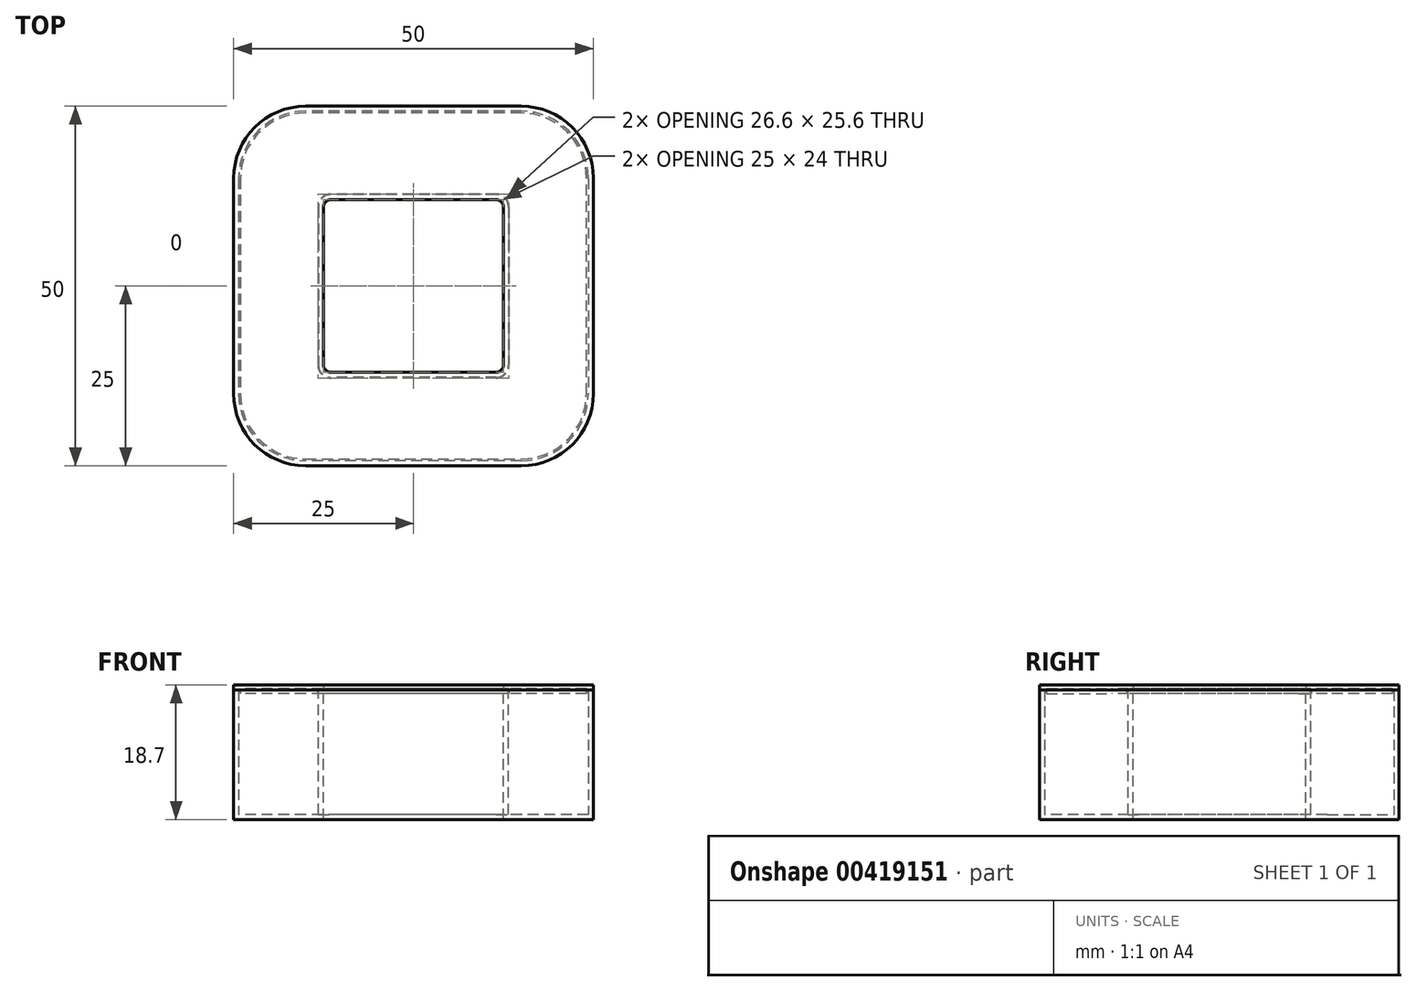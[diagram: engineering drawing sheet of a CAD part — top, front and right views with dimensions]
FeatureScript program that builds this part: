
annotation { "Feature Type Name" : "Feature", "Feature Type Description" : "" }
export const myFeature = defineFeature(function(context is Context, id is Id, definition is map)
    precondition{}
    {
        {
            var Q0;
            Q0=qCreatedBy(makeId("Top.planeOp"),FACE);
            var sketch = newSketch(context, id + "F0", { "sketchPlane" : qUnion([Q0])});
            skLineSegment(sketch, "E0.bottom", {"start": v(15, 25) * mm, "end": v(-15, 25) * mm});
            skLineSegment(sketch, "E0.top", {"start": v(15, -25) * mm, "end": v(-15, -25) * mm});
            skLineSegment(sketch, "E0.left", {"start": v(25, 15) * mm, "end": v(25, -15) * mm});
            skLineSegment(sketch, "E0.right", {"start": v(-25, 15) * mm, "end": v(-25, -15) * mm});
            skPoint(sketch, "E0.middle", {"position": v(0, 0) * mm});
            skPoint(sketch, "E1.visualSharp", {"position": v(-25, 25) * mm});
            skArc(sketch, "E1.filletArc", {"start": v(-15, 25) * mm, "mid": v(-22.07, 22.07) * mm, "end": v(-25, 15) * mm});
            skPoint(sketch, "E2.visualSharp", {"position": v(25, 25) * mm});
            skArc(sketch, "E2.filletArc", {"start": v(25, 15) * mm, "mid": v(22.07, 22.07) * mm, "end": v(15, 25) * mm});
            skPoint(sketch, "E3.visualSharp", {"position": v(25, -25) * mm});
            skArc(sketch, "E3.filletArc", {"start": v(15, -25) * mm, "mid": v(22.07, -22.07) * mm, "end": v(25, -15) * mm});
            skPoint(sketch, "E4.visualSharp", {"position": v(-25, -25) * mm});
            skArc(sketch, "E4.filletArc", {"start": v(-25, -15) * mm, "mid": v(-22.07, -22.07) * mm, "end": v(-15, -25) * mm});
            skSolve(sketch);
        }
        {
            var Q0;
            Q0 = qSketchRegion(id + "F0", true);
            extrude(context, id + "F1", {"entities" : qUnion([Q0]), "depth" : 18 * mm});
        }
        {
            var Q0;
            Q0=makeQuery(id+"F1.opExtrude","CAP_FACE",FACE,{"disambiguationData":[OSD([sQuery(id+"F0.wireOp",EDGE,"E0.bottom"),sQuery(id+"F0.wireOp",EDGE,"E0.top"),sQuery(id+"F0.wireOp",EDGE,"E0.left"),sQuery(id+"F0.wireOp",EDGE,"E0.right"),sQuery(id+"F0.wireOp",EDGE,"E1.filletArc"),sQuery(id+"F0.wireOp",EDGE,"E2.filletArc"),sQuery(id+"F0.wireOp",EDGE,"E3.filletArc"),sQuery(id+"F0.wireOp",EDGE,"E4.filletArc")])],"isStart":false});
            var sketch = newSketch(context, id + "F2", { "sketchPlane" : qUnion([Q0])});
            skLineSegment(sketch, "E5.bottom", {"start": v(11.5, 12) * mm, "end": v(-11.5, 12) * mm});
            skLineSegment(sketch, "E5.top", {"start": v(11.5, -12) * mm, "end": v(-11.5, -12) * mm});
            skLineSegment(sketch, "E5.left", {"start": v(12.5, 11) * mm, "end": v(12.5, -11) * mm});
            skLineSegment(sketch, "E5.right", {"start": v(-12.5, 11) * mm, "end": v(-12.5, -11) * mm});
            skPoint(sketch, "E5.middle", {"position": v(0, 0) * mm});
            skPoint(sketch, "E6.visualSharp", {"position": v(-12.5, 12) * mm});
            skArc(sketch, "E6.filletArc", {"start": v(-11.5, 12) * mm, "mid": v(-12.2, 11.7) * mm, "end": v(-12.5, 11) * mm});
            skPoint(sketch, "E7.visualSharp", {"position": v(12.5, 12) * mm});
            skArc(sketch, "E7.filletArc", {"start": v(12.5, 11) * mm, "mid": v(12.2, 11.7) * mm, "end": v(11.5, 12) * mm});
            skPoint(sketch, "E8.visualSharp", {"position": v(12.5, -12) * mm});
            skArc(sketch, "E8.filletArc", {"start": v(11.5, -12) * mm, "mid": v(12.2, -11.7) * mm, "end": v(12.5, -11) * mm});
            skPoint(sketch, "E9.visualSharp", {"position": v(-12.5, -12) * mm});
            skArc(sketch, "E9.filletArc", {"start": v(-12.5, -11) * mm, "mid": v(-12.2, -11.7) * mm, "end": v(-11.5, -12) * mm});
            skSolve(sketch);
        }
        {
            var Q0;
            Q0=makeQuery(id+"F2.imprint","IMPRINT",FACE,{"disambiguationData":[TD([[makeQuery(id+"F2.imprint","IMPRINT",EDGE,{"derivedFrom":sQuery(id+"F2.wireOp",EDGE,"E5.bottom")}),1.0]])]});
            extrude(context, id + "F3", {"entities" : qUnion([Q0]), "operationType" : NewBodyOperationType.REMOVE, "endBound" : BoundingType.THROUGH_ALL, "oppositeDirection" : true, "depth" : 25 * mm});
        }
        {
            var Q0;
            Q0=makeQuery(id+"F1.opExtrude","CAP_FACE",FACE,{"disambiguationData":[OSD([sQuery(id+"F0.wireOp",EDGE,"E0.bottom"),sQuery(id+"F0.wireOp",EDGE,"E0.top"),sQuery(id+"F0.wireOp",EDGE,"E0.left"),sQuery(id+"F0.wireOp",EDGE,"E0.right"),sQuery(id+"F0.wireOp",EDGE,"E1.filletArc"),sQuery(id+"F0.wireOp",EDGE,"E2.filletArc"),sQuery(id+"F0.wireOp",EDGE,"E3.filletArc"),sQuery(id+"F0.wireOp",EDGE,"E4.filletArc")])],"isStart":false});
            shell(context, id + "F4", {"entities" : qUnion([Q0]), "thickness" : 0.7 * mm});
        }
        {
            var Q0;
            Q0=makeQuery(id+"F1.opExtrude","CAP_FACE",FACE,{"disambiguationData":[OSD([sQuery(id+"F0.wireOp",EDGE,"E0.bottom"),sQuery(id+"F0.wireOp",EDGE,"E0.top"),sQuery(id+"F0.wireOp",EDGE,"E0.left"),sQuery(id+"F0.wireOp",EDGE,"E0.right"),sQuery(id+"F0.wireOp",EDGE,"E1.filletArc"),sQuery(id+"F0.wireOp",EDGE,"E2.filletArc"),sQuery(id+"F0.wireOp",EDGE,"E3.filletArc"),sQuery(id+"F0.wireOp",EDGE,"E4.filletArc")])],"isStart":false});
            var sketch = newSketch(context, id + "F5", { "sketchPlane" : qUnion([Q0])});
            skLineSegment(sketch, "E10.0", {"start": v(-24.3, 15) * mm, "end": v(-24.3, -15) * mm});
            skArc(sketch, "E10.1", {"start": v(-15, 24.3) * mm, "mid": v(-21.58, 21.58) * mm, "end": v(-24.3, 15) * mm});
            skLineSegment(sketch, "E10.2", {"start": v(15, 24.3) * mm, "end": v(-15, 24.3) * mm});
            skArc(sketch, "E10.3", {"start": v(24.3, 15) * mm, "mid": v(21.58, 21.58) * mm, "end": v(15, 24.3) * mm});
            skLineSegment(sketch, "E10.4", {"start": v(24.3, 15) * mm, "end": v(24.3, -15) * mm});
            skArc(sketch, "E10.5", {"start": v(15, -24.3) * mm, "mid": v(21.58, -21.58) * mm, "end": v(24.3, -15) * mm});
            skLineSegment(sketch, "E10.6", {"start": v(15, -24.3) * mm, "end": v(-15, -24.3) * mm});
            skArc(sketch, "E10.7", {"start": v(-24.3, -15) * mm, "mid": v(-21.58, -21.58) * mm, "end": v(-15, -24.3) * mm});
            skLineSegment(sketch, "E10.8", {"start": v(11.5, 12.7) * mm, "end": v(-11.5, 12.7) * mm});
            skArc(sketch, "E10.9", {"start": v(13.2, 11) * mm, "mid": v(12.7, 12.2) * mm, "end": v(11.5, 12.7) * mm});
            skLineSegment(sketch, "E10.10", {"start": v(13.2, 11) * mm, "end": v(13.2, -11) * mm});
            skArc(sketch, "E10.11", {"start": v(11.5, -12.7) * mm, "mid": v(12.7, -12.2) * mm, "end": v(13.2, -11) * mm});
            skLineSegment(sketch, "E10.12", {"start": v(11.5, -12.7) * mm, "end": v(-11.5, -12.7) * mm});
            skArc(sketch, "E10.13", {"start": v(-13.2, -11) * mm, "mid": v(-12.7, -12.2) * mm, "end": v(-11.5, -12.7) * mm});
            skLineSegment(sketch, "E10.14", {"start": v(-13.2, 11) * mm, "end": v(-13.2, -11) * mm});
            skArc(sketch, "E10.15", {"start": v(-11.5, 12.7) * mm, "mid": v(-12.7, 12.2) * mm, "end": v(-13.2, 11) * mm});
            skArc(sketch, "E11.0", {"start": v(23.5, 15) * mm, "mid": v(21.01, 21.01) * mm, "end": v(15, 23.5) * mm});
            skLineSegment(sketch, "E11.1", {"start": v(23.5, 15) * mm, "end": v(23.5, -15) * mm});
            skLineSegment(sketch, "E11.2", {"start": v(15, 23.5) * mm, "end": v(-15, 23.5) * mm});
            skArc(sketch, "E11.3", {"start": v(15, -23.5) * mm, "mid": v(21.01, -21.01) * mm, "end": v(23.5, -15) * mm});
            skArc(sketch, "E11.4", {"start": v(-15, 23.5) * mm, "mid": v(-21.01, 21.01) * mm, "end": v(-23.5, 15) * mm});
            skLineSegment(sketch, "E11.5", {"start": v(-23.5, 15) * mm, "end": v(-23.5, -15) * mm});
            skArc(sketch, "E11.6", {"start": v(-23.5, -15) * mm, "mid": v(-21.01, -21.01) * mm, "end": v(-15, -23.5) * mm});
            skLineSegment(sketch, "E11.7", {"start": v(15, -23.5) * mm, "end": v(-15, -23.5) * mm});
            skArc(sketch, "E12.0", {"start": v(13.3, 11) * mm, "mid": v(12.77, 12.27) * mm, "end": v(11.5, 12.8) * mm});
            skLineSegment(sketch, "E12.1", {"start": v(13.3, 11) * mm, "end": v(13.3, -11) * mm});
            skLineSegment(sketch, "E12.2", {"start": v(11.5, 12.8) * mm, "end": v(-11.5, 12.8) * mm});
            skArc(sketch, "E12.3", {"start": v(11.5, -12.8) * mm, "mid": v(12.77, -12.27) * mm, "end": v(13.3, -11) * mm});
            skArc(sketch, "E12.4", {"start": v(-11.5, 12.8) * mm, "mid": v(-12.77, 12.27) * mm, "end": v(-13.3, 11) * mm});
            skLineSegment(sketch, "E12.5", {"start": v(-13.3, 11) * mm, "end": v(-13.3, -11) * mm});
            skArc(sketch, "E12.6", {"start": v(-13.3, -11) * mm, "mid": v(-12.77, -12.27) * mm, "end": v(-11.5, -12.8) * mm});
            skLineSegment(sketch, "E12.7", {"start": v(11.5, -12.8) * mm, "end": v(-11.5, -12.8) * mm});
            skArc(sketch, "E13.0", {"start": v(-24.05, -15) * mm, "mid": v(-21.4, -21.4) * mm, "end": v(-15, -24.05) * mm});
            skLineSegment(sketch, "E13.1", {"start": v(-24.05, 15) * mm, "end": v(-24.05, -15) * mm});
            skLineSegment(sketch, "E13.2", {"start": v(-15, -24.05) * mm, "end": v(15, -24.05) * mm});
            skArc(sketch, "E13.3", {"start": v(-15, 24.05) * mm, "mid": v(-21.4, 21.4) * mm, "end": v(-24.05, 15) * mm});
            skArc(sketch, "E13.4", {"start": v(15, -24.05) * mm, "mid": v(21.4, -21.4) * mm, "end": v(24.05, -15) * mm});
            skLineSegment(sketch, "E13.5", {"start": v(24.05, -15) * mm, "end": v(24.05, 15) * mm});
            skArc(sketch, "E13.6", {"start": v(24.05, 15) * mm, "mid": v(21.4, 21.4) * mm, "end": v(15, 24.05) * mm});
            skLineSegment(sketch, "E13.7", {"start": v(15, 24.05) * mm, "end": v(-15, 24.05) * mm});
            skSolve(sketch);
        }
        {
            var Q0;
            Q0=makeQuery(id+"F5.imprint","IMPRINT",FACE,{"disambiguationData":[TD([[makeQuery(id+"F5.imprint","IMPRINT",EDGE,{"derivedFrom":sQuery(id+"F5.wireOp",EDGE,"E11.0")}),1.0]])]});
            var Q1;
            Q1=makeQuery(id+"F5.imprint","IMPRINT",FACE,{"disambiguationData":[TD([[makeQuery(id+"F5.imprint","IMPRINT",EDGE,{"derivedFrom":sQuery(id+"F5.wireOp",EDGE,"E11.0")}),-1.0]])]});
            extrude(context, id + "F6", {"entities" : qUnion([Q0, Q1]), "oppositeDirection" : true, "depth" : 0.5 * mm});
        }
        {
            var Q0;
            Q0=makeQuery(id+"F6.opExtrude","CAP_FACE",FACE,{"disambiguationData":[OSD([sQuery(id+"F5.wireOp",EDGE,"E12.0"),sQuery(id+"F5.wireOp",EDGE,"E12.1"),sQuery(id+"F5.wireOp",EDGE,"E12.2"),sQuery(id+"F5.wireOp",EDGE,"E12.3"),sQuery(id+"F5.wireOp",EDGE,"E12.4"),sQuery(id+"F5.wireOp",EDGE,"E12.5"),sQuery(id+"F5.wireOp",EDGE,"E12.6"),sQuery(id+"F5.wireOp",EDGE,"E12.7"),sQuery(id+"F5.wireOp",EDGE,"E13.0"),sQuery(id+"F5.wireOp",EDGE,"E13.1"),sQuery(id+"F5.wireOp",EDGE,"E13.2"),sQuery(id+"F5.wireOp",EDGE,"E13.3"),sQuery(id+"F5.wireOp",EDGE,"E13.4"),sQuery(id+"F5.wireOp",EDGE,"E13.5"),sQuery(id+"F5.wireOp",EDGE,"E13.6"),sQuery(id+"F5.wireOp",EDGE,"E13.7")])],"isStart":true});
            var sketch = newSketch(context, id + "F7", { "sketchPlane" : qUnion([Q0])});
            skArc(sketch, "E14.0", {"start": v(-15, 25) * mm, "mid": v(-22.07, 22.07) * mm, "end": v(-25, 15) * mm});
            skLineSegment(sketch, "E14.1", {"start": v(15, 25) * mm, "end": v(-15, 25) * mm});
            skArc(sketch, "E14.2", {"start": v(25, 15) * mm, "mid": v(22.07, 22.07) * mm, "end": v(15, 25) * mm});
            skLineSegment(sketch, "E14.3", {"start": v(25, 15) * mm, "end": v(25, -15) * mm});
            skArc(sketch, "E14.4", {"start": v(15, -25) * mm, "mid": v(22.07, -22.07) * mm, "end": v(25, -15) * mm});
            skLineSegment(sketch, "E14.5", {"start": v(15, -25) * mm, "end": v(-15, -25) * mm});
            skArc(sketch, "E14.6", {"start": v(-25, -15) * mm, "mid": v(-22.07, -22.07) * mm, "end": v(-15, -25) * mm});
            skLineSegment(sketch, "E14.7", {"start": v(-25, 15) * mm, "end": v(-25, -15) * mm});
            skLineSegment(sketch, "E14.8", {"start": v(-12.5, 11) * mm, "end": v(-12.5, -11) * mm});
            skArc(sketch, "E14.9", {"start": v(-11.5, 12) * mm, "mid": v(-12.2, 11.7) * mm, "end": v(-12.5, 11) * mm});
            skLineSegment(sketch, "E14.10", {"start": v(11.5, 12) * mm, "end": v(-11.5, 12) * mm});
            skArc(sketch, "E14.11", {"start": v(12.5, 11) * mm, "mid": v(12.2, 11.7) * mm, "end": v(11.5, 12) * mm});
            skLineSegment(sketch, "E14.12", {"start": v(12.5, 11) * mm, "end": v(12.5, -11) * mm});
            skArc(sketch, "E14.13", {"start": v(11.5, -12) * mm, "mid": v(12.2, -11.7) * mm, "end": v(12.5, -11) * mm});
            skLineSegment(sketch, "E14.14", {"start": v(11.5, -12) * mm, "end": v(-11.5, -12) * mm});
            skArc(sketch, "E14.15", {"start": v(-12.5, -11) * mm, "mid": v(-12.2, -11.7) * mm, "end": v(-11.5, -12) * mm});
            skSolve(sketch);
        }
        {
            var Q0;
            Q0 = qSketchRegion(id + "F7", true);
            var Q1;
            Q1=makeQuery(id+"F6.opExtrude","CAP_FACE",FACE,{"disambiguationData":[OSD([sQuery(id+"F5.wireOp",EDGE,"E12.0"),sQuery(id+"F5.wireOp",EDGE,"E12.1"),sQuery(id+"F5.wireOp",EDGE,"E12.2"),sQuery(id+"F5.wireOp",EDGE,"E12.3"),sQuery(id+"F5.wireOp",EDGE,"E12.4"),sQuery(id+"F5.wireOp",EDGE,"E12.5"),sQuery(id+"F5.wireOp",EDGE,"E12.6"),sQuery(id+"F5.wireOp",EDGE,"E12.7"),sQuery(id+"F5.wireOp",EDGE,"E13.0"),sQuery(id+"F5.wireOp",EDGE,"E13.1"),sQuery(id+"F5.wireOp",EDGE,"E13.2"),sQuery(id+"F5.wireOp",EDGE,"E13.3"),sQuery(id+"F5.wireOp",EDGE,"E13.4"),sQuery(id+"F5.wireOp",EDGE,"E13.5"),sQuery(id+"F5.wireOp",EDGE,"E13.6"),sQuery(id+"F5.wireOp",EDGE,"E13.7")])],"isStart":false});
            extrude(context, id + "F8", {"entities" : qUnion([Q0, Q1]), "depth" : 0.7 * mm});
        }
    });
